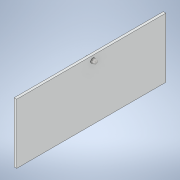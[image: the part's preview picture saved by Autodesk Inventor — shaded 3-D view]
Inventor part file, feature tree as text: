
AUTODESK INVENTOR PART (.ipt)
format: ipt  version: 2021 (Build 250183000, 183)  size: 138,240 bytes
history: imported  units: in
note: dims shown in document units (in); Inventor stores cm internally (conversion verified against a paired STEP export)
features: imported_body x1
ambient origin geometry x8: Origin, YZ Plane, XZ Plane, XY Plane, X Axis, Y Axis, Z Axis, Center Point
bodies: Solid1 (imported_parasolid), Solid2 (imported_parasolid), Body1 (imported_parasolid), Body2 (imported_parasolid)
feature tree (1):
  imported_body  NMx_Import_Brep_tag  [imported B-rep: ~13 faces, bbox_mm=[45.0, 820.0, 2040.0]]
